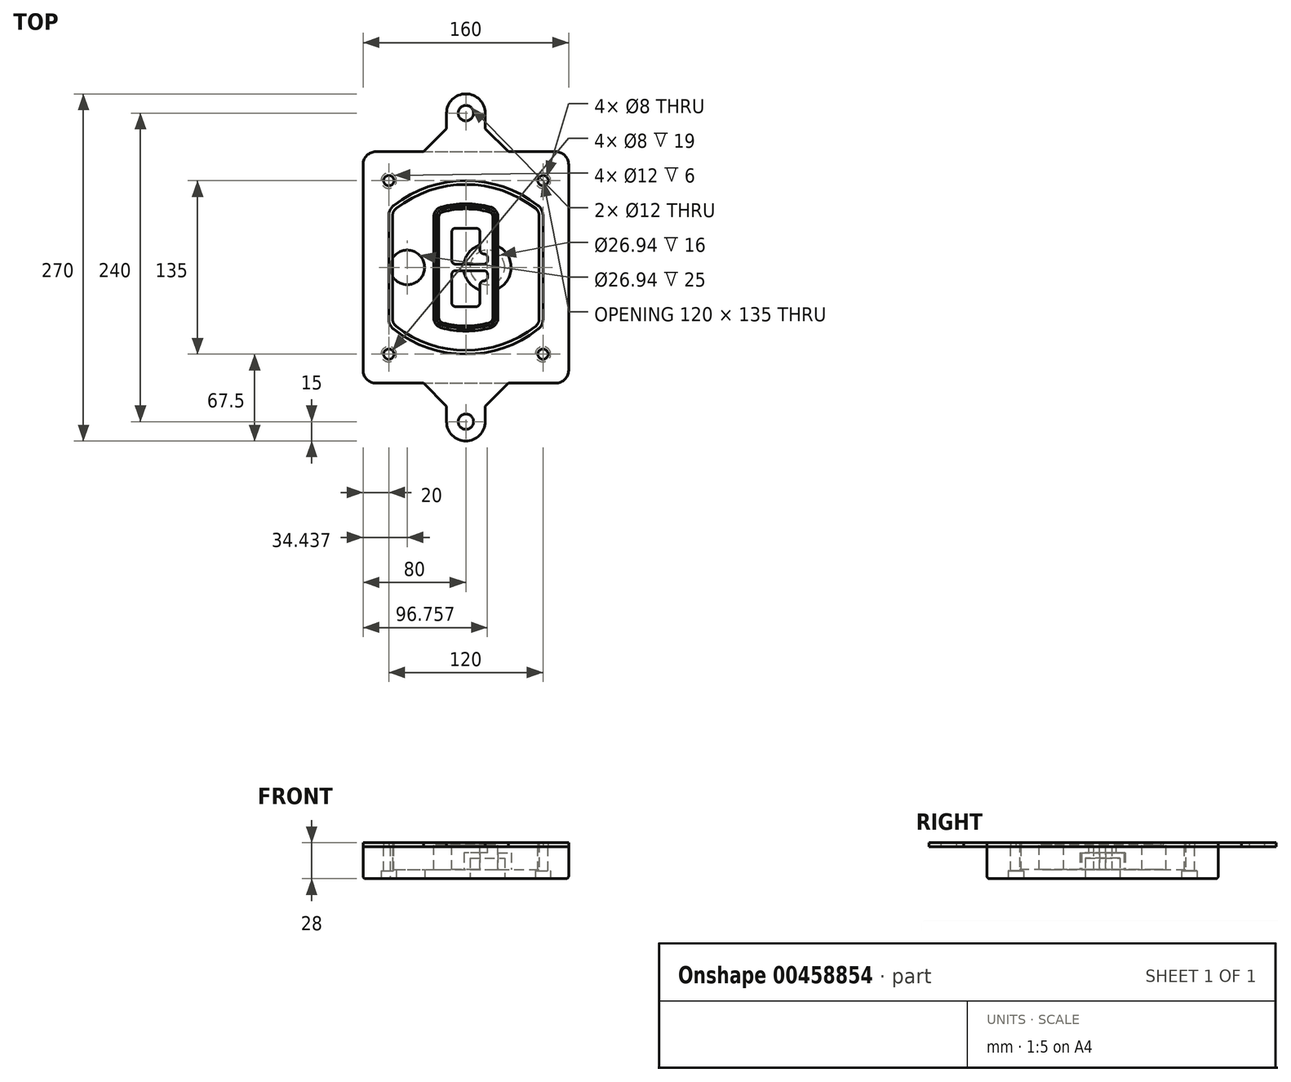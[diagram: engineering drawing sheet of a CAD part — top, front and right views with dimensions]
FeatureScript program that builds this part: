
annotation { "Feature Type Name" : "Feature", "Feature Type Description" : "" }
export const myFeature = defineFeature(function(context is Context, id is Id, definition is map)
    precondition{}
    {
        {
            var Q0;
            Q0=qCreatedBy(makeId("Top.planeOp"),FACE);
            var sketch = newSketch(context, id + "F0", { "sketchPlane" : qUnion([Q0])});
            skPoint(sketch, "E0.rect.middle", {"position": v(0, 0) * mm});
            skLineSegment(sketch, "E1.bottom", {"start": v(-70, -90) * mm, "end": v(70, -90) * mm});
            skLineSegment(sketch, "E1.top", {"start": v(-70, 90) * mm, "end": v(70, 90) * mm});
            skLineSegment(sketch, "E1.left", {"start": v(-80, -80) * mm, "end": v(-80, 80) * mm});
            skLineSegment(sketch, "E1.right", {"start": v(80, -80) * mm, "end": v(80, 80) * mm});
            skLineSegment(sketch, "E2", {"start": v(-80, 90) * mm, "end": v(80, -90) * mm, "construction": true});
            skLineSegment(sketch, "E3", {"start": v(80, 90) * mm, "end": v(-80, -90) * mm, "construction": true});
            skCircle(sketch, "E4", {"center": v(-60, 67.5) * mm, "radius": 4 * mm});
            skCircle(sketch, "E5", {"center": v(60, 67.5) * mm, "radius": 4 * mm});
            skCircle(sketch, "E6", {"center": v(60, -67.5) * mm, "radius": 4 * mm});
            skCircle(sketch, "E7", {"center": v(-60, -67.5) * mm, "radius": 4 * mm});
            skLineSegment(sketch, "E8", {"start": v(-60, 67.5) * mm, "end": v(60, 67.5) * mm, "construction": true});
            skLineSegment(sketch, "E9", {"start": v(60, 67.5) * mm, "end": v(60, -67.5) * mm, "construction": true});
            skLineSegment(sketch, "E10", {"start": v(60, -67.5) * mm, "end": v(-60, -67.5) * mm, "construction": true});
            skLineSegment(sketch, "E11", {"start": v(-60, -67.5) * mm, "end": v(-60, 67.5) * mm, "construction": true});
            skLineSegment(sketch, "E12", {"start": v(-60, 40.3) * mm, "end": v(-60, -40.3) * mm});
            skLineSegment(sketch, "E13", {"start": v(60, 40.3) * mm, "end": v(60, -40.3) * mm});
            skArc(sketch, "E14", {"start": v(56.15, 48.18) * mm, "mid": v(0, 67.5) * mm, "end": v(-56.15, 48.18) * mm});
            skArc(sketch, "E15", {"start": v(-56.15, -48.18) * mm, "mid": v(0, -67.5) * mm, "end": v(56.15, -48.18) * mm});
            skLineSegment(sketch, "E16", {"start": v(-60, 0) * mm, "end": v(60, 0) * mm, "construction": true});
            skPoint(sketch, "E17.visualSharp", {"position": v(-60, -45) * mm});
            skArc(sketch, "E17.filletArc", {"start": v(-60, -40.3) * mm, "mid": v(-58.99, -44.68) * mm, "end": v(-56.15, -48.18) * mm});
            skPoint(sketch, "E18.visualSharp", {"position": v(-60, 45) * mm});
            skArc(sketch, "E18.filletArc", {"start": v(-56.15, 48.18) * mm, "mid": v(-58.99, 44.68) * mm, "end": v(-60, 40.3) * mm});
            skPoint(sketch, "E19.visualSharp", {"position": v(60, 45) * mm});
            skArc(sketch, "E19.filletArc", {"start": v(60, 40.3) * mm, "mid": v(58.99, 44.68) * mm, "end": v(56.15, 48.18) * mm});
            skPoint(sketch, "E20.visualSharp", {"position": v(60, -45) * mm});
            skArc(sketch, "E20.filletArc", {"start": v(56.15, -48.18) * mm, "mid": v(58.99, -44.68) * mm, "end": v(60, -40.3) * mm});
            skPoint(sketch, "E21.visualSharp", {"position": v(-80, 90) * mm});
            skArc(sketch, "E21.filletArc", {"start": v(-70, 90) * mm, "mid": v(-77.07, 87.07) * mm, "end": v(-80, 80) * mm});
            skPoint(sketch, "E22.visualSharp", {"position": v(80, 90) * mm});
            skArc(sketch, "E22.filletArc", {"start": v(80, 80) * mm, "mid": v(77.07, 87.07) * mm, "end": v(70, 90) * mm});
            skPoint(sketch, "E23.visualSharp", {"position": v(80, -90) * mm});
            skArc(sketch, "E23.filletArc", {"start": v(70, -90) * mm, "mid": v(77.07, -87.07) * mm, "end": v(80, -80) * mm});
            skPoint(sketch, "E24.visualSharp", {"position": v(-80, -90) * mm});
            skArc(sketch, "E24.filletArc", {"start": v(-80, -80) * mm, "mid": v(-77.07, -87.07) * mm, "end": v(-70, -90) * mm});
            skArc(sketch, "E25.0", {"start": v(57, 40.3) * mm, "mid": v(56.3, 43.36) * mm, "end": v(54.3, 45.81) * mm});
            skLineSegment(sketch, "E25.1", {"start": v(57, 40.3) * mm, "end": v(57, -40.3) * mm});
            skArc(sketch, "E25.2", {"start": v(54.3, -45.81) * mm, "mid": v(56.3, -43.36) * mm, "end": v(57, -40.3) * mm});
            skArc(sketch, "E25.3", {"start": v(-54.3, -45.81) * mm, "mid": v(0, -64.5) * mm, "end": v(54.3, -45.81) * mm});
            skArc(sketch, "E25.4", {"start": v(-57, -40.3) * mm, "mid": v(-56.3, -43.36) * mm, "end": v(-54.3, -45.81) * mm});
            skArc(sketch, "E25.5", {"start": v(54.3, 45.81) * mm, "mid": v(0, 64.5) * mm, "end": v(-54.3, 45.81) * mm});
            skLineSegment(sketch, "E25.6", {"start": v(-57, 40.3) * mm, "end": v(-57, -40.3) * mm});
            skArc(sketch, "E25.7", {"start": v(-54.3, 45.81) * mm, "mid": v(-56.3, 43.36) * mm, "end": v(-57, 40.3) * mm});
            skArc(sketch, "E26.0", {"start": v(-58.62, 51.33) * mm, "mid": v(-62.58, 46.43) * mm, "end": v(-64, 40.3) * mm});
            skArc(sketch, "E26.1", {"start": v(58.62, 51.33) * mm, "mid": v(0, 71.5) * mm, "end": v(-58.62, 51.33) * mm});
            skArc(sketch, "E26.2", {"start": v(64, 40.3) * mm, "mid": v(62.58, 46.43) * mm, "end": v(58.62, 51.33) * mm});
            skLineSegment(sketch, "E26.3", {"start": v(64, 40.3) * mm, "end": v(64, -40.3) * mm});
            skArc(sketch, "E26.4", {"start": v(58.62, -51.33) * mm, "mid": v(62.58, -46.43) * mm, "end": v(64, -40.3) * mm});
            skLineSegment(sketch, "E26.5", {"start": v(-64, 40.3) * mm, "end": v(-64, -40.3) * mm});
            skArc(sketch, "E26.6", {"start": v(-58.62, -51.33) * mm, "mid": v(0, -71.5) * mm, "end": v(58.62, -51.33) * mm});
            skArc(sketch, "E26.7", {"start": v(-64, -40.3) * mm, "mid": v(-62.58, -46.43) * mm, "end": v(-58.62, -51.33) * mm});
            skSolve(sketch);
        }
        {
            var Q0;
            Q0=makeQuery(id+"F0.imprint","IMPRINT",FACE,{"disambiguationData":[TD([[makeQuery(id+"F0.imprint","IMPRINT",EDGE,{"derivedFrom":sQuery(id+"F0.wireOp",EDGE,"E1.bottom")}),1.0]])]});
            var Q1;
            Q1=makeQuery(id+"F0.imprint","IMPRINT",FACE,{"disambiguationData":[TD([[makeQuery(id+"F0.imprint","IMPRINT",EDGE,{"derivedFrom":sQuery(id+"F0.wireOp",EDGE,"E12")}),1.0]])]});
            var Q2;
            Q2=makeQuery(id+"F0.imprint","IMPRINT",FACE,{"disambiguationData":[TD([[makeQuery(id+"F0.imprint","IMPRINT",EDGE,{"derivedFrom":sQuery(id+"F0.wireOp",EDGE,"E25.0")}),1.0]])]});
            var Q3;
            Q3=makeQuery(id+"F0.imprint","IMPRINT",FACE,{"disambiguationData":[TD([[makeQuery(id+"F0.imprint","IMPRINT",EDGE,{"derivedFrom":sQuery(id+"F0.wireOp",EDGE,"E12")}),-1.0]])]});
            extrude(context, id + "F1", {"entities" : qUnion([Q0, Q1, Q2, Q3]), "oppositeDirection" : true, "depth" : 25 * mm});
        }
        {
            var Q0;
            Q0=makeQuery(id+"F0.imprint","IMPRINT",FACE,{"disambiguationData":[TD([[makeQuery(id+"F0.imprint","IMPRINT",EDGE,{"derivedFrom":sQuery(id+"F0.wireOp",EDGE,"E12")}),1.0]])]});
            extrude(context, id + "F2", {"entities" : qUnion([Q0]), "operationType" : NewBodyOperationType.ADD, "depth" : 3 * mm});
        }
        {
            var Q0;
            Q0=makeQuery(id+"F0.imprint","IMPRINT",FACE,{"disambiguationData":[TD([[makeQuery(id+"F0.imprint","IMPRINT",EDGE,{"derivedFrom":sQuery(id+"F0.wireOp",EDGE,"E25.0")}),1.0]])]});
            extrude(context, id + "F3", {"entities" : qUnion([Q0]), "operationType" : NewBodyOperationType.REMOVE, "oppositeDirection" : true, "depth" : 18 * mm});
        }
        {
            var Q0;
            Q0=makeQuery(id+"F2.opExtrude","CAP_FACE",FACE,{"disambiguationData":[OSD([sQuery(id+"F0.wireOp",EDGE,"E12"),sQuery(id+"F0.wireOp",EDGE,"E13"),sQuery(id+"F0.wireOp",EDGE,"E14"),sQuery(id+"F0.wireOp",EDGE,"E15"),sQuery(id+"F0.wireOp",EDGE,"E17.filletArc"),sQuery(id+"F0.wireOp",EDGE,"E18.filletArc"),sQuery(id+"F0.wireOp",EDGE,"E19.filletArc"),sQuery(id+"F0.wireOp",EDGE,"E20.filletArc"),sQuery(id+"F0.wireOp",EDGE,"E25.0"),sQuery(id+"F0.wireOp",EDGE,"E25.1"),sQuery(id+"F0.wireOp",EDGE,"E25.2"),sQuery(id+"F0.wireOp",EDGE,"E25.3"),sQuery(id+"F0.wireOp",EDGE,"E25.4"),sQuery(id+"F0.wireOp",EDGE,"E25.5"),sQuery(id+"F0.wireOp",EDGE,"E25.6"),sQuery(id+"F0.wireOp",EDGE,"E25.7")])],"isStart":false});
            var sketch = newSketch(context, id + "F4", { "sketchPlane" : qUnion([Q0])});
            skArc(sketch, "E27.0", {"start": v(-19.08, -46.97) * mm, "mid": v(0, -49.5) * mm, "end": v(19.08, -46.97) * mm});
            skArc(sketch, "E28.0", {"start": v(19.08, 46.97) * mm, "mid": v(0, 49.5) * mm, "end": v(-19.08, 46.97) * mm});
            skLineSegment(sketch, "E29", {"start": v(-25, 39.25) * mm, "end": v(-25, -39.25) * mm});
            skLineSegment(sketch, "E30", {"start": v(25, 39.25) * mm, "end": v(25, -39.25) * mm});
            skLineSegment(sketch, "E31", {"start": v(-25, 45.1) * mm, "end": v(25, 45.1) * mm, "construction": true});
            skLineSegment(sketch, "E32", {"start": v(-25, -45.1) * mm, "end": v(25, -45.1) * mm, "construction": true});
            skPoint(sketch, "E33.visualSharp", {"position": v(-25, 45.1) * mm});
            skArc(sketch, "E33.filletArc", {"start": v(-19.08, 46.97) * mm, "mid": v(-23.35, 44.11) * mm, "end": v(-25, 39.25) * mm});
            skPoint(sketch, "E34.visualSharp", {"position": v(25, 45.1) * mm});
            skArc(sketch, "E34.filletArc", {"start": v(25, 39.25) * mm, "mid": v(23.35, 44.11) * mm, "end": v(19.08, 46.97) * mm});
            skPoint(sketch, "E35.visualSharp", {"position": v(25, -45.1) * mm});
            skArc(sketch, "E35.filletArc", {"start": v(19.08, -46.97) * mm, "mid": v(23.35, -44.11) * mm, "end": v(25, -39.25) * mm});
            skPoint(sketch, "E36.visualSharp", {"position": v(-25, -45.1) * mm});
            skArc(sketch, "E36.filletArc", {"start": v(-25, -39.25) * mm, "mid": v(-23.35, -44.11) * mm, "end": v(-19.08, -46.97) * mm});
            skArc(sketch, "E37.0", {"start": v(54.3, 45.81) * mm, "mid": v(0, 64.5) * mm, "end": v(-54.3, 45.81) * mm});
            skArc(sketch, "E37.1", {"start": v(-54.3, 45.81) * mm, "mid": v(-56.3, 43.36) * mm, "end": v(-57, 40.3) * mm});
            skLineSegment(sketch, "E37.2", {"start": v(-57, 40.3) * mm, "end": v(-57, -40.3) * mm});
            skArc(sketch, "E37.3", {"start": v(-57, -40.3) * mm, "mid": v(-56.3, -43.36) * mm, "end": v(-54.3, -45.81) * mm});
            skArc(sketch, "E37.4", {"start": v(-54.3, -45.81) * mm, "mid": v(0, -64.5) * mm, "end": v(54.3, -45.81) * mm});
            skArc(sketch, "E37.5", {"start": v(54.3, -45.81) * mm, "mid": v(56.3, -43.36) * mm, "end": v(57, -40.3) * mm});
            skLineSegment(sketch, "E37.6", {"start": v(57, 40.3) * mm, "end": v(57, -40.3) * mm});
            skArc(sketch, "E37.7", {"start": v(57, 40.3) * mm, "mid": v(56.3, 43.36) * mm, "end": v(54.3, 45.81) * mm});
            skLineSegment(sketch, "E38.0", {"start": v(23, 39.25) * mm, "end": v(23, -39.25) * mm});
            skArc(sketch, "E38.1", {"start": v(18.56, -45.04) * mm, "mid": v(21.76, -42.9) * mm, "end": v(23, -39.25) * mm});
            skArc(sketch, "E38.2", {"start": v(-18.56, -45.04) * mm, "mid": v(0, -47.5) * mm, "end": v(18.56, -45.04) * mm});
            skArc(sketch, "E38.3", {"start": v(-23, -39.25) * mm, "mid": v(-21.76, -42.9) * mm, "end": v(-18.56, -45.04) * mm});
            skLineSegment(sketch, "E38.4", {"start": v(-23, 39.25) * mm, "end": v(-23, -39.25) * mm});
            skArc(sketch, "E38.5", {"start": v(23, 39.25) * mm, "mid": v(21.76, 42.9) * mm, "end": v(18.56, 45.04) * mm});
            skArc(sketch, "E38.6", {"start": v(-18.56, 45.04) * mm, "mid": v(-21.76, 42.9) * mm, "end": v(-23, 39.25) * mm});
            skArc(sketch, "E38.7", {"start": v(18.56, 45.04) * mm, "mid": v(0, 47.5) * mm, "end": v(-18.56, 45.04) * mm});
            skArc(sketch, "E39.0", {"start": v(21, 39.25) * mm, "mid": v(20.18, 41.68) * mm, "end": v(18.04, 43.1) * mm});
            skLineSegment(sketch, "E39.1", {"start": v(21, 39.25) * mm, "end": v(21, -39.25) * mm});
            skArc(sketch, "E39.2", {"start": v(18.04, -43.1) * mm, "mid": v(20.18, -41.68) * mm, "end": v(21, -39.25) * mm});
            skArc(sketch, "E39.3", {"start": v(-18.04, -43.1) * mm, "mid": v(0, -45.5) * mm, "end": v(18.04, -43.1) * mm});
            skArc(sketch, "E39.4", {"start": v(-21, -39.25) * mm, "mid": v(-20.18, -41.68) * mm, "end": v(-18.04, -43.1) * mm});
            skArc(sketch, "E39.5", {"start": v(18.04, 43.1) * mm, "mid": v(0, 45.5) * mm, "end": v(-18.04, 43.1) * mm});
            skLineSegment(sketch, "E39.6", {"start": v(-21, 39.25) * mm, "end": v(-21, -39.25) * mm});
            skArc(sketch, "E39.7", {"start": v(-18.04, 43.1) * mm, "mid": v(-20.18, 41.68) * mm, "end": v(-21, 39.25) * mm});
            skLineSegment(sketch, "E40", {"start": v(-25, 0) * mm, "end": v(25, 0) * mm, "construction": true});
            skLineSegment(sketch, "E41", {"start": v(-11, 5.5) * mm, "end": v(-11, 27.5) * mm});
            skLineSegment(sketch, "E42", {"start": v(-8, 30.5) * mm, "end": v(8, 30.5) * mm});
            skLineSegment(sketch, "E43", {"start": v(11, 27.5) * mm, "end": v(11, 13.5) * mm});
            skLineSegment(sketch, "E44", {"start": v(14, 10.5) * mm, "end": v(14, 10.5) * mm});
            skLineSegment(sketch, "E45", {"start": v(17, 7.5) * mm, "end": v(17, 5.5) * mm});
            skLineSegment(sketch, "E46", {"start": v(14, 2.5) * mm, "end": v(-8, 2.5) * mm});
            skPoint(sketch, "E47.visualSharp", {"position": v(-11, 30.5) * mm});
            skArc(sketch, "E47.filletArc", {"start": v(-8, 30.5) * mm, "mid": v(-10.12, 29.62) * mm, "end": v(-11, 27.5) * mm});
            skPoint(sketch, "E48.visualSharp", {"position": v(11, 30.5) * mm});
            skArc(sketch, "E48.filletArc", {"start": v(11, 27.5) * mm, "mid": v(10.12, 29.62) * mm, "end": v(8, 30.5) * mm});
            skPoint(sketch, "E49.visualSharp", {"position": v(11, 10.5) * mm});
            skArc(sketch, "E49.filletArc", {"start": v(11, 13.5) * mm, "mid": v(11.88, 11.38) * mm, "end": v(14, 10.5) * mm});
            skPoint(sketch, "E50.visualSharp", {"position": v(17, 10.5) * mm});
            skArc(sketch, "E50.filletArc", {"start": v(17, 7.5) * mm, "mid": v(16.12, 9.62) * mm, "end": v(14, 10.5) * mm});
            skPoint(sketch, "E51.visualSharp", {"position": v(17, 2.5) * mm});
            skArc(sketch, "E51.filletArc", {"start": v(14, 2.5) * mm, "mid": v(16.12, 3.38) * mm, "end": v(17, 5.5) * mm});
            skPoint(sketch, "E52.visualSharp", {"position": v(-11, 2.5) * mm});
            skArc(sketch, "E52.filletArc", {"start": v(-11, 5.5) * mm, "mid": v(-10.12, 3.38) * mm, "end": v(-8, 2.5) * mm});
            skLineSegment(sketch, "E53.0.MirrorCS", {"start": v(14, -2.5) * mm, "end": v(-8, -2.5) * mm});
            skArc(sketch, "E54.0.MirrorCS", {"start": v(-11, -5.5) * mm, "mid": v(-10.12, -3.38) * mm, "end": v(-8, -2.5) * mm});
            skLineSegment(sketch, "E55.0.MirrorCS", {"start": v(-11, -5.5) * mm, "end": v(-11, -27.5) * mm});
            skArc(sketch, "E56.0.MirrorCS", {"start": v(-8, -30.5) * mm, "mid": v(-10.12, -29.62) * mm, "end": v(-11, -27.5) * mm});
            skLineSegment(sketch, "E57.0.MirrorCS", {"start": v(-8, -30.5) * mm, "end": v(8, -30.5) * mm});
            skArc(sketch, "E58.0.MirrorCS", {"start": v(11, -27.5) * mm, "mid": v(10.12, -29.62) * mm, "end": v(8, -30.5) * mm});
            skLineSegment(sketch, "E59.0.MirrorCS", {"start": v(11, -27.5) * mm, "end": v(11, -13.5) * mm});
            skArc(sketch, "E60.0.MirrorCS", {"start": v(11, -13.5) * mm, "mid": v(11.88, -11.38) * mm, "end": v(14, -10.5) * mm});
            skArc(sketch, "E61.0.MirrorCS", {"start": v(17, -7.5) * mm, "mid": v(16.12, -9.62) * mm, "end": v(14, -10.5) * mm});
            skLineSegment(sketch, "E62.0.MirrorCS", {"start": v(17, -7.5) * mm, "end": v(17, -5.5) * mm});
            skArc(sketch, "E63.0.MirrorCS", {"start": v(14, -2.5) * mm, "mid": v(16.12, -3.38) * mm, "end": v(17, -5.5) * mm});
            skSolve(sketch);
        }
        {
            var Q0;
            Q0=makeQuery(id+"F4.imprint","IMPRINT",FACE,{"disambiguationData":[TD([[makeQuery(id+"F4.imprint","IMPRINT",EDGE,{"derivedFrom":sQuery(id+"F4.wireOp",EDGE,"E27.0")}),1.0]])]});
            var Q1;
            Q1=makeQuery(id+"F4.imprint","IMPRINT",FACE,{"disambiguationData":[TD([[makeQuery(id+"F4.imprint","IMPRINT",EDGE,{"derivedFrom":sQuery(id+"F4.wireOp",EDGE,"E38.0")}),-1.0]])]});
            var Q2;
            Q2=makeQuery(id+"F4.imprint","IMPRINT",FACE,{"disambiguationData":[TD([[makeQuery(id+"F4.imprint","IMPRINT",EDGE,{"derivedFrom":sQuery(id+"F4.wireOp",EDGE,"E39.0")}),1.0]])]});
            extrude(context, id + "F5", {"entities" : qUnion([Q0, Q1, Q2]), "operationType" : NewBodyOperationType.ADD, "endBound" : BoundingType.UP_TO_NEXT, "oppositeDirection" : true, "depth" : 25 * mm});
        }
        {
            var Q0;
            Q0=makeQuery(id+"F4.imprint","IMPRINT",FACE,{"disambiguationData":[TD([[makeQuery(id+"F4.imprint","IMPRINT",EDGE,{"derivedFrom":sQuery(id+"F4.wireOp",EDGE,"E38.0")}),-1.0]])]});
            extrude(context, id + "F6", {"entities" : qUnion([Q0]), "operationType" : NewBodyOperationType.REMOVE, "oppositeDirection" : true, "depth" : 2 * mm});
        }
        {
            var Q0;
            Q0=makeQuery(id+"F1.opExtrude","CAP_FACE",FACE,{"disambiguationData":[OSD([sQuery(id+"F0.wireOp",EDGE,"E1.bottom"),sQuery(id+"F0.wireOp",EDGE,"E1.top"),sQuery(id+"F0.wireOp",EDGE,"E1.left"),sQuery(id+"F0.wireOp",EDGE,"E1.right"),sQuery(id+"F0.wireOp",EDGE,"E4"),sQuery(id+"F0.wireOp",EDGE,"E5"),sQuery(id+"F0.wireOp",EDGE,"E6"),sQuery(id+"F0.wireOp",EDGE,"E7"),sQuery(id+"F0.wireOp",EDGE,"E21.filletArc"),sQuery(id+"F0.wireOp",EDGE,"E22.filletArc"),sQuery(id+"F0.wireOp",EDGE,"E23.filletArc"),sQuery(id+"F0.wireOp",EDGE,"E24.filletArc")])],"isStart":false});
            var sketch = newSketch(context, id + "F7", { "sketchPlane" : qUnion([Q0])});
            skCircle(sketch, "E64", {"center": v(16.76, 0) * mm, "radius": 13.47 * mm});
            skCircle(sketch, "E65", {"center": v(-45.56, 0) * mm, "radius": 13.47 * mm});
            skLineSegment(sketch, "E66", {"start": v(80, 0) * mm, "end": v(-80, 0) * mm});
            skCircle(sketch, "E67", {"center": v(16.76, 0) * mm, "radius": 18.47 * mm});
            skCircle(sketch, "E68", {"center": v(60, -67.5) * mm, "radius": 6 * mm});
            skCircle(sketch, "E69", {"center": v(-60, -67.5) * mm, "radius": 6 * mm});
            skCircle(sketch, "E70", {"center": v(-60, 67.5) * mm, "radius": 6 * mm});
            skCircle(sketch, "E71", {"center": v(60, 67.5) * mm, "radius": 6 * mm});
            skSolve(sketch);
        }
        {
            var Q0;
            {var subQ1=sQuery(id+"F7.wireOp",EDGE,"E66");var subQ4=sQuery(id+"F7.wireOp",EDGE,"E64");var subQ6=makeQuery(id+"F7.imprint","INTERSECT",VERTEX,{"disambiguationData":[OD(0.0)],"derivedFrom":[subQ4,subQ1]});Q0=makeQuery(id+"F7.imprint","IMPRINT",FACE,{"disambiguationData":[TD([[makeQuery(id+"F7.imprint","IMPRINT",EDGE,{"disambiguationData":[TD([[subQ6,-1.0]])],"derivedFrom":subQ4}),-1.0]])]});}
            var Q1;
            {var subQ0=sQuery(id+"F7.wireOp",EDGE,"E66");var subQ1=sQuery(id+"F7.wireOp",EDGE,"E64");var subQ3=makeQuery(id+"F7.imprint","INTERSECT",VERTEX,{"disambiguationData":[OD(0.0)],"derivedFrom":[subQ1,subQ0]});Q1=makeQuery(id+"F7.imprint","IMPRINT",FACE,{"disambiguationData":[TD([[makeQuery(id+"F7.imprint","IMPRINT",EDGE,{"disambiguationData":[TD([[subQ3,-1.0]])],"derivedFrom":subQ1}),1.0]])]});}
            var Q2;
            {var subQ0=sQuery(id+"F7.wireOp",EDGE,"E66");var subQ1=sQuery(id+"F7.wireOp",EDGE,"E64");var subQ3=makeQuery(id+"F7.imprint","INTERSECT",VERTEX,{"disambiguationData":[OD(0.0)],"derivedFrom":[subQ1,subQ0]});Q2=makeQuery(id+"F7.imprint","IMPRINT",FACE,{"disambiguationData":[TD([[makeQuery(id+"F7.imprint","IMPRINT",EDGE,{"disambiguationData":[TD([[subQ3,1.0]])],"derivedFrom":subQ1}),1.0]])]});}
            var Q3;
            {var subQ1=sQuery(id+"F7.wireOp",EDGE,"E66");var subQ4=sQuery(id+"F7.wireOp",EDGE,"E64");var subQ6=makeQuery(id+"F7.imprint","INTERSECT",VERTEX,{"disambiguationData":[OD(0.0)],"derivedFrom":[subQ4,subQ1]});Q3=makeQuery(id+"F7.imprint","IMPRINT",FACE,{"disambiguationData":[TD([[makeQuery(id+"F7.imprint","IMPRINT",EDGE,{"disambiguationData":[TD([[subQ6,1.0]])],"derivedFrom":subQ4}),-1.0]])]});}
            extrude(context, id + "F8", {"entities" : qUnion([Q0, Q1, Q2, Q3]), "operationType" : NewBodyOperationType.ADD, "oppositeDirection" : true, "depth" : 20 * mm});
        }
        {
            var Q0;
            {var subQ0=sQuery(id+"F7.wireOp",EDGE,"E66");var subQ1=sQuery(id+"F7.wireOp",EDGE,"E64");var subQ3=makeQuery(id+"F7.imprint","INTERSECT",VERTEX,{"disambiguationData":[OD(0.0)],"derivedFrom":[subQ1,subQ0]});Q0=makeQuery(id+"F7.imprint","IMPRINT",FACE,{"disambiguationData":[TD([[makeQuery(id+"F7.imprint","IMPRINT",EDGE,{"disambiguationData":[TD([[subQ3,-1.0]])],"derivedFrom":subQ1}),1.0]])]});}
            var Q1;
            {var subQ0=sQuery(id+"F7.wireOp",EDGE,"E66");var subQ1=sQuery(id+"F7.wireOp",EDGE,"E64");var subQ3=makeQuery(id+"F7.imprint","INTERSECT",VERTEX,{"disambiguationData":[OD(0.0)],"derivedFrom":[subQ1,subQ0]});Q1=makeQuery(id+"F7.imprint","IMPRINT",FACE,{"disambiguationData":[TD([[makeQuery(id+"F7.imprint","IMPRINT",EDGE,{"disambiguationData":[TD([[subQ3,1.0]])],"derivedFrom":subQ1}),1.0]])]});}
            extrude(context, id + "F9", {"entities" : qUnion([Q0, Q1]), "operationType" : NewBodyOperationType.REMOVE, "oppositeDirection" : true, "depth" : 16 * mm});
        }
        {
            var Q0;
            {var subQ0=sQuery(id+"F7.wireOp",EDGE,"E66");var subQ1=sQuery(id+"F7.wireOp",EDGE,"E65");var subQ3=makeQuery(id+"F7.imprint","INTERSECT",VERTEX,{"disambiguationData":[OD(0.0)],"derivedFrom":[subQ1,subQ0]});Q0=makeQuery(id+"F7.imprint","IMPRINT",FACE,{"disambiguationData":[TD([[makeQuery(id+"F7.imprint","IMPRINT",EDGE,{"disambiguationData":[TD([[subQ3,-1.0]])],"derivedFrom":subQ1}),1.0]])]});}
            var Q1;
            {var subQ0=sQuery(id+"F7.wireOp",EDGE,"E66");var subQ1=sQuery(id+"F7.wireOp",EDGE,"E65");var subQ3=makeQuery(id+"F7.imprint","INTERSECT",VERTEX,{"disambiguationData":[OD(0.0)],"derivedFrom":[subQ1,subQ0]});Q1=makeQuery(id+"F7.imprint","IMPRINT",FACE,{"disambiguationData":[TD([[makeQuery(id+"F7.imprint","IMPRINT",EDGE,{"disambiguationData":[TD([[subQ3,1.0]])],"derivedFrom":subQ1}),1.0]])]});}
            extrude(context, id + "F10", {"entities" : qUnion([Q0, Q1]), "operationType" : NewBodyOperationType.REMOVE, "oppositeDirection" : true, "depth" : 25 * mm});
        }
        {
            var Q0;
            Q0=makeQuery(id+"F7.imprint","IMPRINT",FACE,{"disambiguationData":[TD([[makeQuery(id+"F7.imprint","IMPRINT",EDGE,{"derivedFrom":sQuery(id+"F7.wireOp",EDGE,"E68")}),1.0]])]});
            var Q1;
            Q1=makeQuery(id+"F7.imprint","IMPRINT",FACE,{"disambiguationData":[TD([[makeQuery(id+"F7.imprint","IMPRINT",EDGE,{"derivedFrom":makeQuery(id+"F1.opExtrude","CAP_EDGE",EDGE,{"disambiguationData":[OSD([sQuery(id+"F0.wireOp",EDGE,"E5")])],"isStart":false})}),-1.0]])]});
            var Q2;
            Q2=makeQuery(id+"F7.imprint","IMPRINT",FACE,{"disambiguationData":[TD([[makeQuery(id+"F7.imprint","IMPRINT",EDGE,{"derivedFrom":sQuery(id+"F7.wireOp",EDGE,"E69")}),1.0]])]});
            var Q3;
            Q3=makeQuery(id+"F7.imprint","IMPRINT",FACE,{"disambiguationData":[TD([[makeQuery(id+"F7.imprint","IMPRINT",EDGE,{"derivedFrom":makeQuery(id+"F1.opExtrude","CAP_EDGE",EDGE,{"disambiguationData":[OSD([sQuery(id+"F0.wireOp",EDGE,"E4")])],"isStart":false})}),-1.0]])]});
            var Q4;
            Q4=makeQuery(id+"F7.imprint","IMPRINT",FACE,{"disambiguationData":[TD([[makeQuery(id+"F7.imprint","IMPRINT",EDGE,{"derivedFrom":sQuery(id+"F7.wireOp",EDGE,"E70")}),1.0]])]});
            var Q5;
            Q5=makeQuery(id+"F7.imprint","IMPRINT",FACE,{"disambiguationData":[TD([[makeQuery(id+"F7.imprint","IMPRINT",EDGE,{"derivedFrom":makeQuery(id+"F1.opExtrude","CAP_EDGE",EDGE,{"disambiguationData":[OSD([sQuery(id+"F0.wireOp",EDGE,"E7")])],"isStart":false})}),-1.0]])]});
            var Q6;
            Q6=makeQuery(id+"F7.imprint","IMPRINT",FACE,{"disambiguationData":[TD([[makeQuery(id+"F7.imprint","IMPRINT",EDGE,{"derivedFrom":sQuery(id+"F7.wireOp",EDGE,"E71")}),1.0]])]});
            var Q7;
            Q7=makeQuery(id+"F7.imprint","IMPRINT",FACE,{"disambiguationData":[TD([[makeQuery(id+"F7.imprint","IMPRINT",EDGE,{"derivedFrom":makeQuery(id+"F1.opExtrude","CAP_EDGE",EDGE,{"disambiguationData":[OSD([sQuery(id+"F0.wireOp",EDGE,"E6")])],"isStart":false})}),-1.0]])]});
            extrude(context, id + "F11", {"entities" : qUnion([Q0, Q1, Q2, Q3, Q4, Q5, Q6, Q7]), "operationType" : NewBodyOperationType.REMOVE, "oppositeDirection" : true, "depth" : 6 * mm});
        }
        {
            var Q0;
            Q0=makeQuery(id+"F1.opExtrude","CAP_EDGE",EDGE,{"disambiguationData":[OSD([sQuery(id+"F0.wireOp",EDGE,"E1.bottom")])],"isStart":false});
            fillet(context, id + "F12", {"entities" : qUnion([Q0]), "radius" : 2 * mm, "tangentPropagation" : true, "allowEdgeOverflow" : false});
        }
        {
            var Q0;
            Q0=qCreatedBy(makeId("Top.planeOp"),FACE);
            var sketch = newSketch(context, id + "F13", { "sketchPlane" : qUnion([Q0])});
            skLineSegment(sketch, "E72.0", {"start": v(-70, 90) * mm, "end": v(70, 90) * mm});
            skArc(sketch, "E72.1", {"start": v(-70, 90) * mm, "mid": v(-77.07, 87.07) * mm, "end": v(-80, 80) * mm});
            skLineSegment(sketch, "E72.2", {"start": v(-80, -80) * mm, "end": v(-80, 80) * mm});
            skArc(sketch, "E72.3", {"start": v(56.15, 48.18) * mm, "mid": v(0, 67.5) * mm, "end": v(-56.15, 48.18) * mm});
            skArc(sketch, "E72.4", {"start": v(-56.15, 48.18) * mm, "mid": v(-58.99, 44.68) * mm, "end": v(-60, 40.3) * mm});
            skLineSegment(sketch, "E72.5", {"start": v(-60, 40.3) * mm, "end": v(-60, -40.3) * mm});
            skArc(sketch, "E72.6", {"start": v(-60, -40.3) * mm, "mid": v(-58.99, -44.68) * mm, "end": v(-56.15, -48.18) * mm});
            skArc(sketch, "E72.7", {"start": v(-56.15, -48.18) * mm, "mid": v(0, -67.5) * mm, "end": v(56.15, -48.18) * mm});
            skLineSegment(sketch, "E72.8", {"start": v(60, 40.3) * mm, "end": v(60, -40.3) * mm});
            skArc(sketch, "E72.9", {"start": v(60, 40.3) * mm, "mid": v(58.99, 44.68) * mm, "end": v(56.15, 48.18) * mm});
            skArc(sketch, "E72.10", {"start": v(56.15, -48.18) * mm, "mid": v(58.99, -44.68) * mm, "end": v(60, -40.3) * mm});
            skLineSegment(sketch, "E72.11", {"start": v(80, -80) * mm, "end": v(80, 80) * mm});
            skArc(sketch, "E72.12", {"start": v(80, 80) * mm, "mid": v(77.07, 87.07) * mm, "end": v(70, 90) * mm});
            skLineSegment(sketch, "E72.13", {"start": v(-70, -90) * mm, "end": v(70, -90) * mm});
            skArc(sketch, "E72.14", {"start": v(70, -90) * mm, "mid": v(77.07, -87.07) * mm, "end": v(80, -80) * mm});
            skArc(sketch, "E72.15", {"start": v(-80, -80) * mm, "mid": v(-77.07, -87.07) * mm, "end": v(-70, -90) * mm});
            skCircle(sketch, "E72.16", {"center": v(-60, 67.5) * mm, "radius": 4 * mm});
            skCircle(sketch, "E72.17", {"center": v(60, 67.5) * mm, "radius": 4 * mm});
            skCircle(sketch, "E72.18", {"center": v(60, -67.5) * mm, "radius": 4 * mm});
            skCircle(sketch, "E72.19", {"center": v(-60, -67.5) * mm, "radius": 4 * mm});
            skLineSegment(sketch, "E73", {"start": v(0, 90) * mm, "end": v(0, 120) * mm, "construction": true});
            skPoint(sketch, "E73.endSnap0", {"position": v(0, 90) * mm});
            skArc(sketch, "E74", {"start": v(15, 120) * mm, "mid": v(0, 135) * mm, "end": v(-15, 120) * mm});
            skLineSegment(sketch, "E75", {"start": v(-15, 120) * mm, "end": v(-15, 108) * mm});
            skLineSegment(sketch, "E76", {"start": v(15, 120) * mm, "end": v(15, 108) * mm});
            skLineSegment(sketch, "E77", {"start": v(15, 108) * mm, "end": v(33, 90) * mm});
            skLineSegment(sketch, "E78", {"start": v(-15, 108) * mm, "end": v(-33, 90) * mm});
            skCircle(sketch, "E79", {"center": v(0, 120) * mm, "radius": 6 * mm});
            skLineSegment(sketch, "E80", {"start": v(-80, 0) * mm, "end": v(80, 0) * mm, "construction": true});
            skLineSegment(sketch, "E81.MirrorCS", {"start": v(-15, -108) * mm, "end": v(-33, -90) * mm});
            skLineSegment(sketch, "E82.MirrorCS", {"start": v(-15, -120) * mm, "end": v(-15, -108) * mm});
            skArc(sketch, "E83.MirrorCS", {"start": v(15, -120) * mm, "mid": v(0, -135) * mm, "end": v(-15, -120) * mm});
            skCircle(sketch, "E84.MirrorC", {"center": v(0, -120) * mm, "radius": 6 * mm});
            skLineSegment(sketch, "E85.MirrorCS", {"start": v(15, -120) * mm, "end": v(15, -108) * mm});
            skLineSegment(sketch, "E86.MirrorCS", {"start": v(15, -108) * mm, "end": v(33, -90) * mm});
            skLineSegment(sketch, "E87.MirrorCS", {"start": v(0, -90) * mm, "end": v(0, -120) * mm, "construction": true});
            skSolve(sketch);
        }
        {
            var Q0;
            Q0 = qSketchRegion(id + "F13", true);
            var Q1;
            Q1=makeQuery(id+"F2.opExtrude","CAP_FACE",FACE,{"disambiguationData":[OSD([sQuery(id+"F0.wireOp",EDGE,"E12"),sQuery(id+"F0.wireOp",EDGE,"E13"),sQuery(id+"F0.wireOp",EDGE,"E14"),sQuery(id+"F0.wireOp",EDGE,"E15"),sQuery(id+"F0.wireOp",EDGE,"E17.filletArc"),sQuery(id+"F0.wireOp",EDGE,"E18.filletArc"),sQuery(id+"F0.wireOp",EDGE,"E19.filletArc"),sQuery(id+"F0.wireOp",EDGE,"E20.filletArc"),sQuery(id+"F0.wireOp",EDGE,"E25.0"),sQuery(id+"F0.wireOp",EDGE,"E25.1"),sQuery(id+"F0.wireOp",EDGE,"E25.2"),sQuery(id+"F0.wireOp",EDGE,"E25.3"),sQuery(id+"F0.wireOp",EDGE,"E25.4"),sQuery(id+"F0.wireOp",EDGE,"E25.5"),sQuery(id+"F0.wireOp",EDGE,"E25.6"),sQuery(id+"F0.wireOp",EDGE,"E25.7")])],"isStart":false});
            extrude(context, id + "F14", {"entities" : qUnion([Q0]), "endBound" : BoundingType.UP_TO_SURFACE, "endBoundEntityFace" : qUnion([Q1]), "depth" : 25 * mm});
        }
    });
